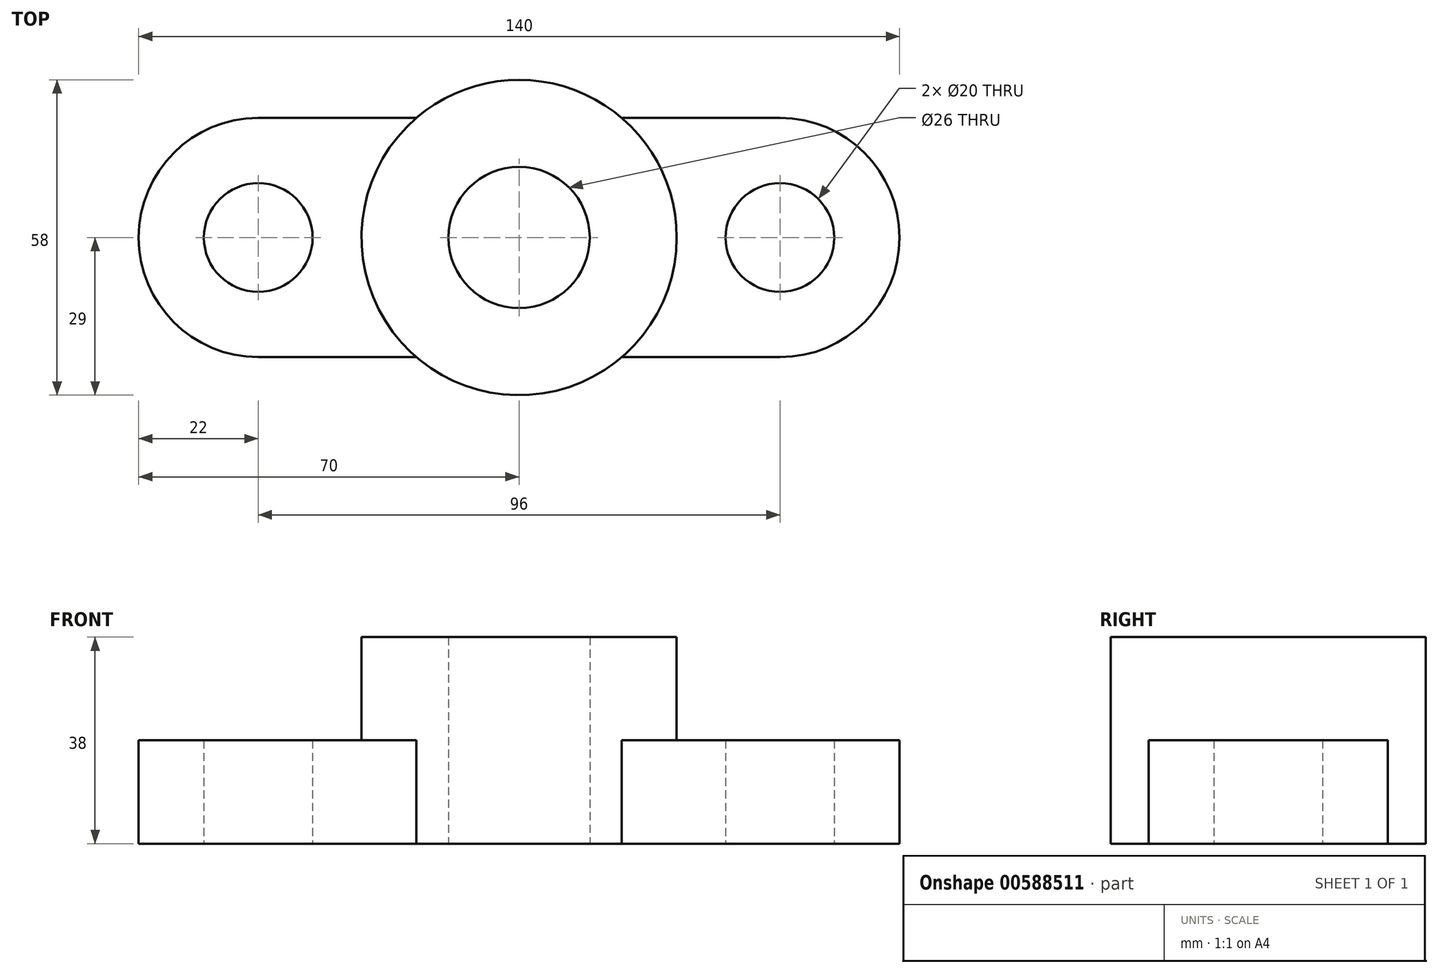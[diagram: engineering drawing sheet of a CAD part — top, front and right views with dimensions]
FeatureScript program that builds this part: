
annotation { "Feature Type Name" : "Feature", "Feature Type Description" : "" }
export const myFeature = defineFeature(function(context is Context, id is Id, definition is map)
    precondition{}
    {
        {
            var Q0;
            Q0=qCreatedBy(makeId("Top.planeOp"),FACE);
            var sketch = newSketch(context, id + "F0", { "sketchPlane" : qUnion([Q0])});
            skCircle(sketch, "E0", {"center": v(0, 0) * mm, "radius": 29 * mm});
            skCircle(sketch, "E1", {"center": v(0, 0) * mm, "radius": 13 * mm});
            skCircle(sketch, "E2", {"center": v(-48, 0) * mm, "radius": 10 * mm});
            skArc(sketch, "E3", {"start": v(-48, 22) * mm, "mid": v(-70, 0) * mm, "end": v(-48, -22) * mm});
            skCircle(sketch, "E4", {"center": v(48, 0) * mm, "radius": 10 * mm});
            skArc(sketch, "E5", {"start": v(48, -22) * mm, "mid": v(70, 0) * mm, "end": v(48, 22) * mm});
            skLineSegment(sketch, "E6", {"start": v(-48, -22) * mm, "end": v(-18.9, -22) * mm});
            skLineSegment(sketch, "E7", {"start": v(-48, 22) * mm, "end": v(-18.9, 22) * mm});
            skLineSegment(sketch, "E8.trimOffspring", {"start": v(18.9, -22) * mm, "end": v(48, -22) * mm});
            skLineSegment(sketch, "E9.trimOffspring", {"start": v(18.9, 22) * mm, "end": v(48, 22) * mm});
            skSolve(sketch);
        }
        {
            var Q0;
            Q0=makeQuery(id+"F0.imprint","IMPRINT",FACE,{"disambiguationData":[TD([[makeQuery(id+"F0.imprint","IMPRINT",EDGE,{"derivedFrom":sQuery(id+"F0.wireOp",EDGE,"E2")}),-1.0]])]});
            var Q1;
            Q1=makeQuery(id+"F0.imprint","IMPRINT",FACE,{"disambiguationData":[TD([[makeQuery(id+"F0.imprint","IMPRINT",EDGE,{"derivedFrom":sQuery(id+"F0.wireOp",EDGE,"E4")}),-1.0]])]});
            var Q2;
            Q2=makeQuery(id+"F0.imprint","IMPRINT",FACE,{"disambiguationData":[TD([[makeQuery(id+"F0.imprint","IMPRINT",EDGE,{"derivedFrom":sQuery(id+"F0.wireOp",EDGE,"E1")}),-1.0]])]});
            extrude(context, id + "F1", {"entities" : qUnion([Q0, Q1, Q2]), "depth" : 19 * mm, "offsetDistance" : 25 * mm});
        }
        {
            var Q0;
            Q0=makeQuery(id+"F0.imprint","IMPRINT",FACE,{"disambiguationData":[TD([[makeQuery(id+"F0.imprint","IMPRINT",EDGE,{"derivedFrom":sQuery(id+"F0.wireOp",EDGE,"E1")}),-1.0]])]});
            extrude(context, id + "F2", {"entities" : qUnion([Q0]), "operationType" : NewBodyOperationType.ADD, "depth" : 38 * mm, "offsetDistance" : 25 * mm});
        }
    });
